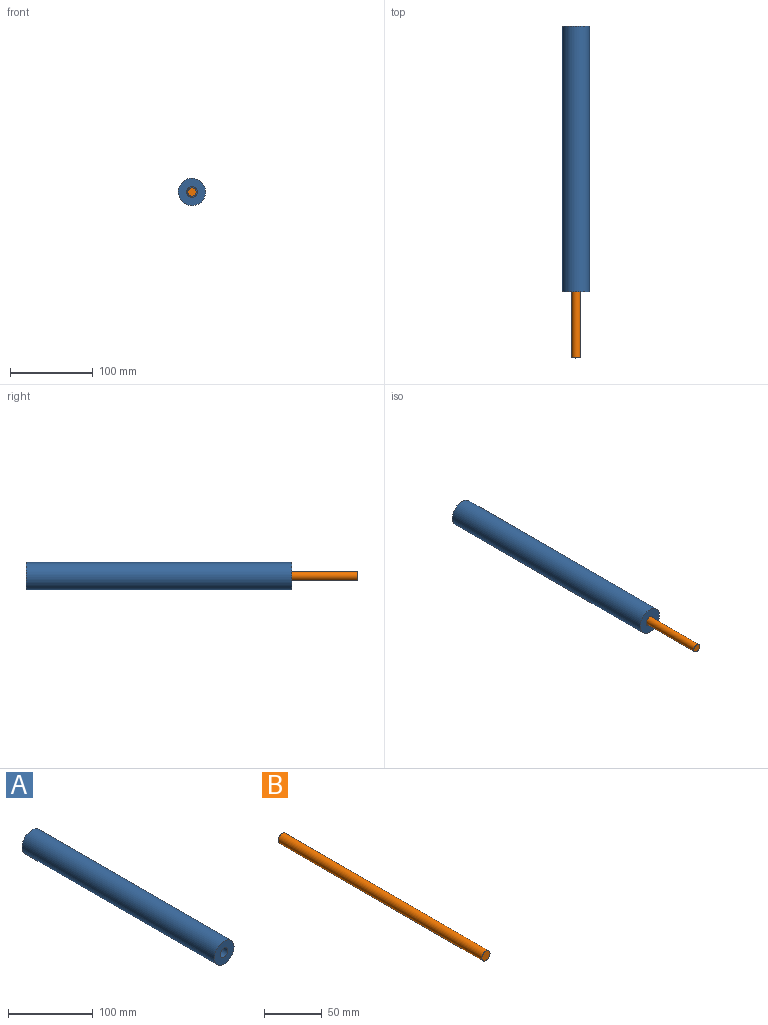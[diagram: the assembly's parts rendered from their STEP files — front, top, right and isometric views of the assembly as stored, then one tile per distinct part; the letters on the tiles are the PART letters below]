
ASSEMBLY  parts=2 mates=1
PART A: 5 faces, bbox 32.8x320x32.8 mm
  f0: cylinder r=16.42mm len=320mm, axis (0,1,0), area 33018.8mm2, adj f1,f2
  f1: plane 32.84x32.84mm, normal (0,-1,0), area 717.7mm2, adj f0,f3
  f2: plane 32.84x32.84mm, normal (0,1,0), area 847.3mm2, adj f0
  f3: cylinder r=6.42mm len=310mm, axis (0,1,0), area 12509.1mm2, adj f1,f4
  f4: plane 12.84x12.84mm, normal (0,-1,0), area 129.6mm2, adj f3
PART B: 3 faces, bbox 10x250x10 mm
  f0: cylinder r=5mm len=250mm, axis (0,1,0), area 7854mm2, adj f1,f2
  f1: plane 10x10mm, normal (0,-1,0), area 78.5mm2, adj f0
  f2: plane 10x10mm, normal (0,1,0), area 78.5mm2, adj f0
PLACE A rot(axis=(0,1,0),12.9deg) t=(-33.19,-13.08,46.26)mm
PLACE B rot(axis=(0.99,0,-0.11),180deg) t=(-33.19,-413.08,46.26)mm
MATE slider B.f0 <-> A.f0  axis (0,1,0) through (-33.19,-163.08,46.26)mm
